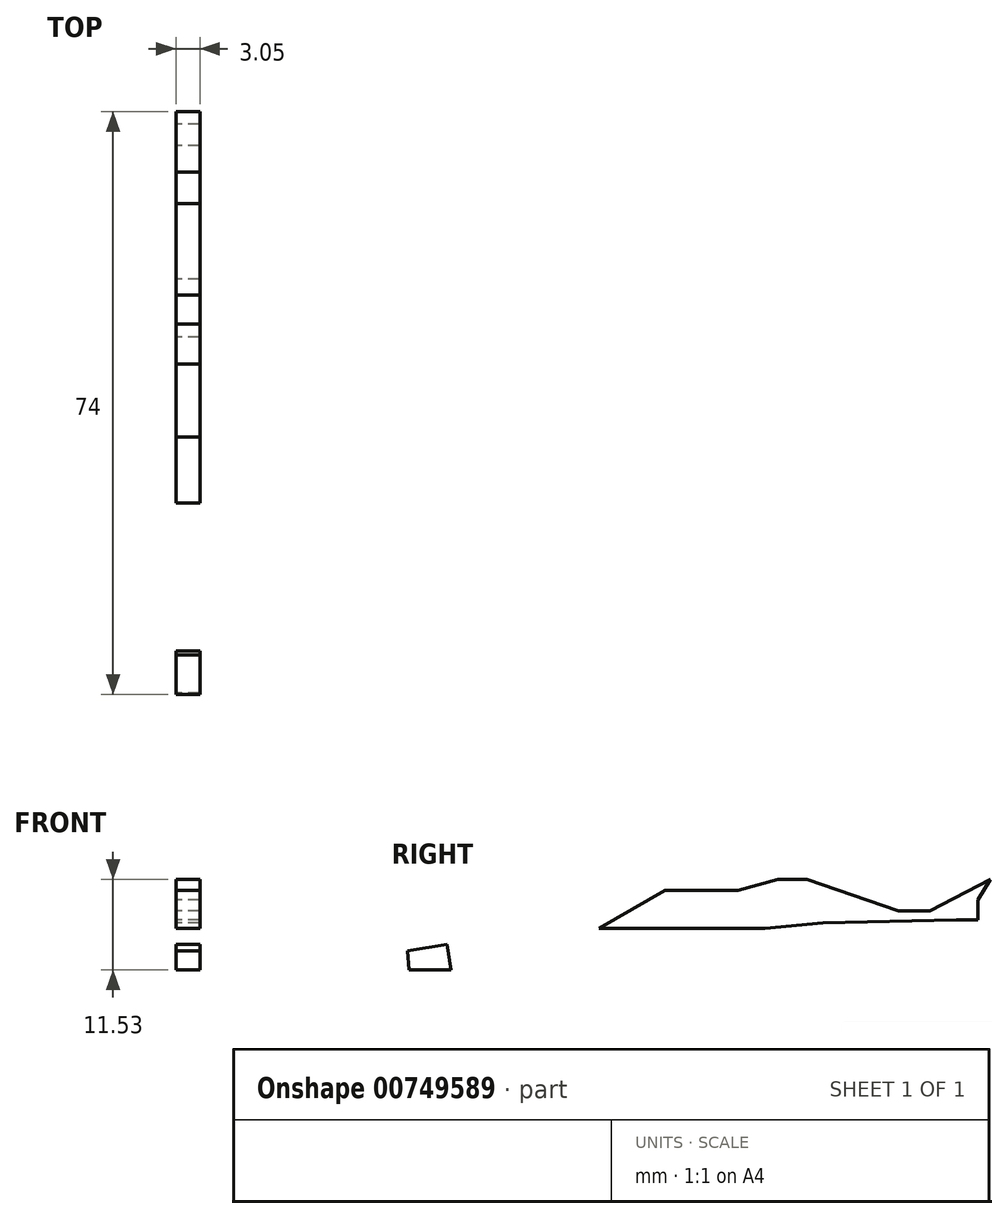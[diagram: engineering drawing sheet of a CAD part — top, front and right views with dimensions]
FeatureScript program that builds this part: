
annotation { "Feature Type Name" : "Feature", "Feature Type Description" : "" }
export const myFeature = defineFeature(function(context is Context, id is Id, definition is map)
    precondition{}
    {
        {
            var Q0;
            Q0=qCreatedBy(makeId("Right.planeOp"),FACE);
            var sketch = newSketch(context, id + "F0", { "sketchPlane" : qUnion([Q0])});
            skLineSegment(sketch, "E0", {"start": v(-49.85, 31.35) * mm, "end": v(-17.95, 31.35) * mm});
            skArc(sketch, "E1", {"start": v(-17.95, 31.35) * mm, "mid": v(-6.72, 32.3) * mm, "end": v(-14.98, 39.96) * mm});
            skLineSegment(sketch, "E2", {"start": v(-5.42, 32.3) * mm, "end": v(2.7, 34.3) * mm});
            skPoint(sketch, "E2.startSnap0", {"position": v(-6.72, 32.3) * mm});
            skLineSegment(sketch, "E3", {"start": v(2.7, 34.3) * mm, "end": v(2.7, 39.18) * mm});
            skLineSegment(sketch, "E4", {"start": v(2.7, 39.18) * mm, "end": v(0, 39.4) * mm});
            skLineSegment(sketch, "E5", {"start": v(0, 39.4) * mm, "end": v(0, 44.92) * mm});
            skLineSegment(sketch, "E6", {"start": v(0, 44.92) * mm, "end": v(2.7, 44.92) * mm});
            skLineSegment(sketch, "E7", {"start": v(2.7, 44.92) * mm, "end": v(2.7, 47.5) * mm});
            skLineSegment(sketch, "E8", {"start": v(2.7, 47.5) * mm, "end": v(4.27, 50.1) * mm});
            skLineSegment(sketch, "E9", {"start": v(4.27, 50.1) * mm, "end": v(-0.65, 47.5) * mm});
            skLineSegment(sketch, "E10", {"start": v(-0.65, 47.5) * mm, "end": v(-3.37, 46.08) * mm});
            skLineSegment(sketch, "E11", {"start": v(-3.37, 46.08) * mm, "end": v(-7.4, 46.08) * mm});
            skLineSegment(sketch, "E12", {"start": v(-7.4, 46.08) * mm, "end": v(-19.01, 50.1) * mm});
            skLineSegment(sketch, "E13", {"start": v(-19.01, 50.1) * mm, "end": v(-36.53, 50.1) * mm});
            skLineSegment(sketch, "E14", {"start": v(-36.53, 50.1) * mm, "end": v(-45.58, 44.92) * mm});
            skLineSegment(sketch, "E15", {"start": v(-45.58, 44.92) * mm, "end": v(-69.73, 41.02) * mm});
            skLineSegment(sketch, "E16", {"start": v(-69.73, 41.02) * mm, "end": v(-71.4, 37.88) * mm});
            skLineSegment(sketch, "E17", {"start": v(-71.4, 37.88) * mm, "end": v(-71.4, 34.3) * mm});
            skLineSegment(sketch, "E18", {"start": v(-71.4, 34.3) * mm, "end": v(-69.73, 31.58) * mm});
            skLineSegment(sketch, "E19", {"start": v(-69.73, 31.58) * mm, "end": v(-62.6, 31.15) * mm});
            skArc(sketch, "E20", {"start": v(-62.6, 31.15) * mm, "mid": v(-51, 32.73) * mm, "end": v(-59.96, 40.26) * mm});
            skLineSegment(sketch, "E21", {"start": v(-45.41, 34.11) * mm, "end": v(-46.85, 43) * mm});
            skLineSegment(sketch, "E22", {"start": v(-45.41, 34.11) * mm, "end": v(-26.98, 34.11) * mm});
            skLineSegment(sketch, "E23", {"start": v(-26.98, 34.11) * mm, "end": v(-24.37, 43.87) * mm});
            skLineSegment(sketch, "E24", {"start": v(-24.37, 43.87) * mm, "end": v(-45.41, 43.87) * mm});
            skLineSegment(sketch, "E25", {"start": v(-45.41, 43.87) * mm, "end": v(-37.03, 48.67) * mm});
            skLineSegment(sketch, "E26", {"start": v(-37.03, 48.67) * mm, "end": v(-27.77, 48.67) * mm});
            skPoint(sketch, "E26.endSnap0", {"position": v(-27.77, 50.1) * mm});
            skLineSegment(sketch, "E27", {"start": v(-27.77, 48.67) * mm, "end": v(-24.37, 43.87) * mm});
            skLineSegment(sketch, "E28", {"start": v(-24.37, 43.87) * mm, "end": v(-16.98, 44.53) * mm});
            skLineSegment(sketch, "E29", {"start": v(-16.98, 44.53) * mm, "end": v(-22.7, 50.1) * mm});
            skLineSegment(sketch, "E30", {"start": v(-22.7, 50.1) * mm, "end": v(-27.77, 48.67) * mm});
            skLineSegment(sketch, "E31", {"start": v(-16.98, 44.53) * mm, "end": v(0, 44.92) * mm});
            skLineSegment(sketch, "E32", {"start": v(-64.73, 41.83) * mm, "end": v(-64.2, 38.57) * mm});
            skLineSegment(sketch, "E33", {"start": v(-64.2, 38.57) * mm, "end": v(-69.56, 38.57) * mm});
            skLineSegment(sketch, "E34", {"start": v(-69.56, 38.57) * mm, "end": v(-69.73, 41.02) * mm});
            skSolve(sketch);
        }
        {
            var Q0;
            Q0 = qSketchRegion(id + "F0", true);
            extrude(context, id + "F1", {"entities" : qUnion([Q0]), "depth" : 3.05 * mm, "offsetDistance" : 25.4 * mm});
        }
    });
